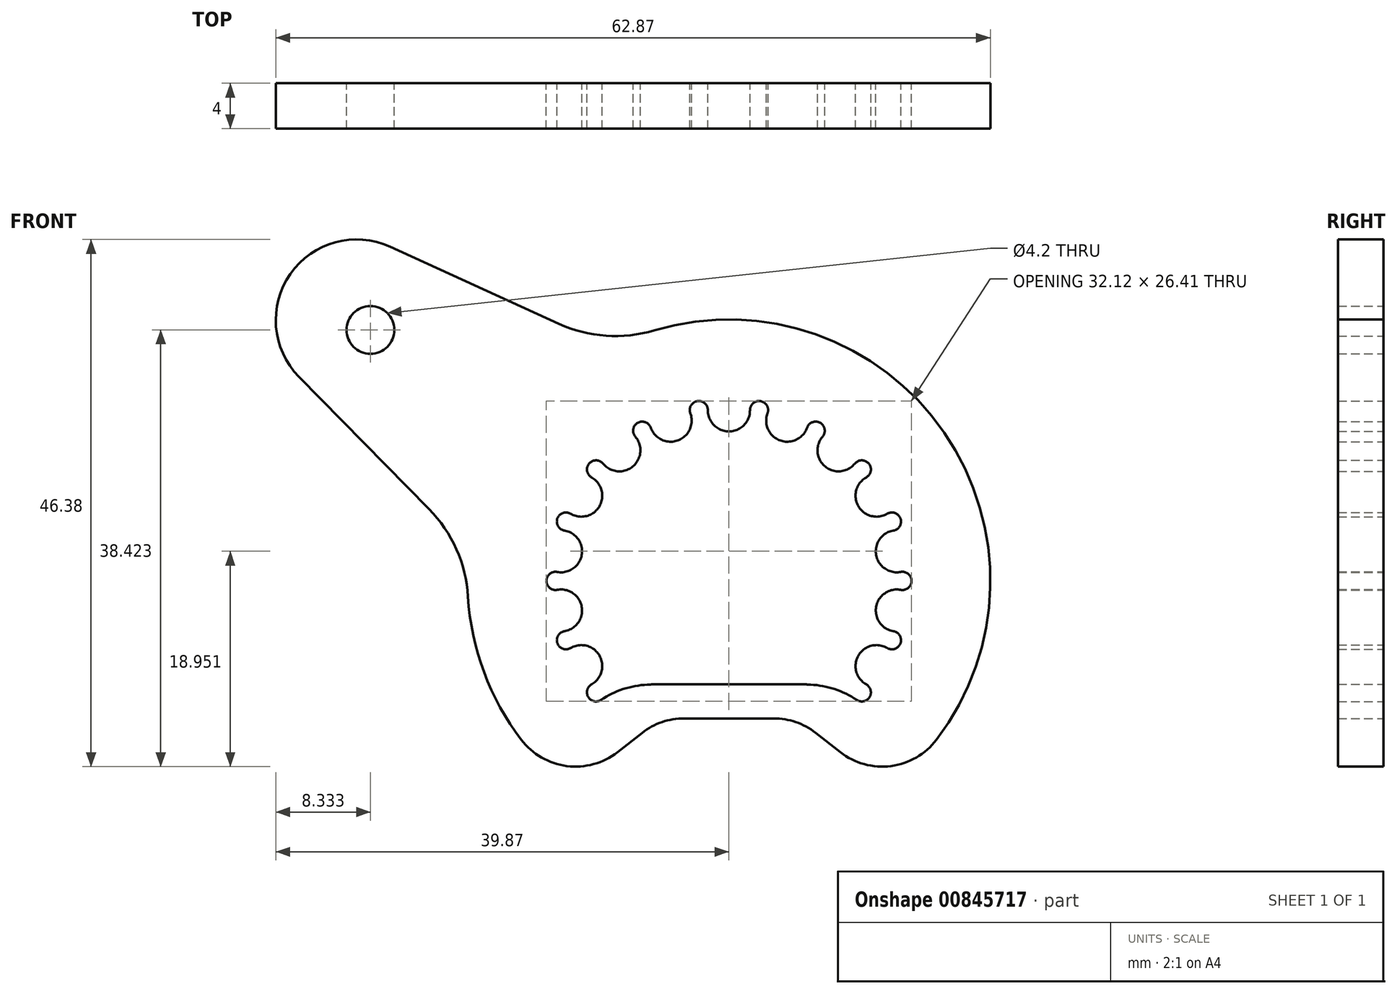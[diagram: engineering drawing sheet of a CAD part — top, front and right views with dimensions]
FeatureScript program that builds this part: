
annotation { "Feature Type Name" : "Feature", "Feature Type Description" : "" }
export const myFeature = defineFeature(function(context is Context, id is Id, definition is map)
    precondition{}
    {
        {
            var Q0;
            Q0=qCreatedBy(makeId("Front.planeOp"),FACE);
            var sketch = newSketch(context, id + "F0", { "sketchPlane" : qUnion([Q0])});
            skArc(sketch, "E0", {"start": v(-22.96, -1.37) * mm, "mid": v(-21.55, -8.03) * mm, "end": v(-18.26, -13.99) * mm});
            skLineSegment(sketch, "E1", {"start": v(-3.93, -12.1) * mm, "end": v(3.93, -12.1) * mm});
            skLineSegment(sketch, "E2", {"start": v(0, 0) * mm, "end": v(0, -12.1) * mm, "construction": true});
            skLineSegment(sketch, "E3", {"start": v(7.63, -13.37) * mm, "end": v(9.8, -15.07) * mm});
            skLineSegment(sketch, "E4", {"start": v(0, 0) * mm, "end": v(-32.77, 22.94) * mm, "construction": true});
            skLineSegment(sketch, "E5.trimOffspring", {"start": v(-28.05, 7.74) * mm, "end": v(-38.36, 14.96) * mm, "construction": true});
            skArc(sketch, "E6", {"start": v(-40.75, 28.54) * mm, "mid": v(-42.37, 21.25) * mm, "end": v(-38.36, 14.96) * mm, "construction": true});
            skArc(sketch, "E7.MirrorCS", {"start": v(-40.75, 28.54) * mm, "mid": v(-34.46, 32.54) * mm, "end": v(-27.17, 30.93) * mm, "construction": true});
            skLineSegment(sketch, "E8.MirrorCS", {"start": v(-16.87, 23.72) * mm, "end": v(-27.17, 30.93) * mm, "construction": true});
            skLineSegment(sketch, "E9.MirrorCS", {"start": v(-7.63, -13.37) * mm, "end": v(-9.8, -15.07) * mm});
            skArc(sketch, "E10.trimOffspring", {"start": v(18.26, -13.99) * mm, "mid": v(18.94, 13.05) * mm, "end": v(-6.56, 22.04) * mm});
            skLineSegment(sketch, "E11", {"start": v(-11.93, -9.1) * mm, "end": v(11.93, -9.1) * mm, "construction": true});
            skArc(sketch, "E12", {"start": v(11.43, -9.72) * mm, "mid": v(0, 15) * mm, "end": v(-11.43, -9.72) * mm, "construction": true});
            skPoint(sketch, "E13.visualSharp", {"position": v(-13.94, -18.3) * mm});
            skArc(sketch, "E13.filletArc", {"start": v(-18.26, -13.99) * mm, "mid": v(-14.25, -16.3) * mm, "end": v(-9.8, -15.07) * mm});
            skPoint(sketch, "E14.visualSharp", {"position": v(-6, -12.1) * mm});
            skArc(sketch, "E14.filletArc", {"start": v(-3.93, -12.1) * mm, "mid": v(-5.89, -12.42) * mm, "end": v(-7.63, -13.37) * mm});
            skPoint(sketch, "E15.visualSharp", {"position": v(6, -12.1) * mm});
            skArc(sketch, "E15.filletArc", {"start": v(7.63, -13.37) * mm, "mid": v(5.89, -12.42) * mm, "end": v(3.93, -12.1) * mm});
            skPoint(sketch, "E16.visualSharp", {"position": v(13.94, -18.3) * mm});
            skArc(sketch, "E16.filletArc", {"start": v(9.8, -15.07) * mm, "mid": v(14.25, -16.3) * mm, "end": v(18.26, -13.99) * mm});
            skPoint(sketch, "E17.visualSharp", {"position": v(-22.66, 3.96) * mm});
            skArc(sketch, "E17.filletArc", {"start": v(-22.96, -1.37) * mm, "mid": v(-24.46, 3.77) * mm, "end": v(-28.05, 7.74) * mm, "construction": true});
            skPoint(sketch, "E18.visualSharp", {"position": v(-11.47, 19.93) * mm});
            skArc(sketch, "E18.filletArc", {"start": v(-16.87, 23.72) * mm, "mid": v(-11.9, 21.7) * mm, "end": v(-6.56, 22.04) * mm});
            skArc(sketch, "E19", {"start": v(-30.99, 25.48) * mm, "mid": v(-35.3, 24.72) * mm, "end": v(-34.54, 20.4) * mm, "construction": true});
            skLineSegment(sketch, "E20", {"start": v(-28.43, -16.34) * mm, "end": v(42.41, -16.34) * mm, "construction": true});
            skLineSegment(sketch, "E21", {"start": v(-31.95, 22.37) * mm, "end": v(-26.35, 30.36) * mm, "construction": true});
            skArc(sketch, "E22", {"start": v(-24.72, 29.2) * mm, "mid": v(-26.21, 29.54) * mm, "end": v(-27.5, 28.72) * mm, "construction": true});
            skLineSegment(sketch, "E23", {"start": v(-32.8, 29.57) * mm, "end": v(-14.34, 29.57) * mm, "construction": true});
            skLineSegment(sketch, "E24", {"start": v(6, -12.1) * mm, "end": v(6, -9.1) * mm, "construction": true});
            skArc(sketch, "E25.trimOffspring", {"start": v(7.18, -9.13) * mm, "mid": v(6.6, -9.1) * mm, "end": v(6, -9.1) * mm});
            skArc(sketch, "E26.MirrorCS", {"start": v(-7.18, -9.13) * mm, "mid": v(-6.6, -9.1) * mm, "end": v(-6, -9.1) * mm});
            skLineSegment(sketch, "E27", {"start": v(-6, -9.1) * mm, "end": v(6, -9.1) * mm});
            skLineSegment(sketch, "E28", {"start": v(-34.54, 20.4) * mm, "end": v(-28, 15.82) * mm, "construction": true});
            skLineSegment(sketch, "E29", {"start": v(-30.99, 25.48) * mm, "end": v(-24.43, 20.9) * mm, "construction": true});
            skArc(sketch, "E30", {"start": v(-28, 15.82) * mm, "mid": v(-23.67, 16.58) * mm, "end": v(-24.43, 20.9) * mm, "construction": true});
            skArc(sketch, "E31.0", {"start": v(-29.82, 29.4) * mm, "mid": v(-38.58, 27.02) * mm, "end": v(-37.83, 17.96) * mm});
            skLineSegment(sketch, "E32", {"start": v(-37.83, 17.96) * mm, "end": v(-26.38, 6.33) * mm});
            skPoint(sketch, "E32.endSnap0", {"position": v(-24.46, 3.77) * mm});
            skPoint(sketch, "E33.orphan", {"position": v(-24.46, 4.38) * mm});
            skArc(sketch, "E34", {"start": v(-22.96, -1.37) * mm, "mid": v(-23.97, 2.79) * mm, "end": v(-26.38, 6.33) * mm});
            skLineSegment(sketch, "E35.MirrorCS", {"start": v(-29.82, 29.4) * mm, "end": v(-14.97, 22.63) * mm});
            skArc(sketch, "E36.MirrorCS", {"start": v(-6.56, 22.04) * mm, "mid": v(-10.82, 21.57) * mm, "end": v(-14.97, 22.63) * mm, "construction": true});
            skPoint(sketch, "E37.orphan", {"position": v(-16.87, 23.72) * mm});
            skLineSegment(sketch, "E38", {"start": v(0, 0) * mm, "end": v(13, -7.5) * mm, "construction": true});
            skArc(sketch, "E39", {"start": v(13.93, -5.9) * mm, "mid": v(11.39, -6.58) * mm, "end": v(12.08, -9.11) * mm});
            skLineSegment(sketch, "E40", {"start": v(0, 0) * mm, "end": v(14.77, -2.6) * mm, "construction": true});
            skArc(sketch, "E41", {"start": v(15.11, -0.79) * mm, "mid": v(12.95, -2.28) * mm, "end": v(14.47, -4.43) * mm});
            skArc(sketch, "E42", {"start": v(13.93, -5.9) * mm, "mid": v(15.1, -5.5) * mm, "end": v(14.47, -4.43) * mm});
            skArc(sketch, "E43", {"start": v(13.3, -5.67) * mm, "mid": v(14.17, -5.16) * mm, "end": v(13.83, -4.2) * mm, "construction": true});
            skArc(sketch, "E44.MirrorCS", {"start": v(12.08, -9.11) * mm, "mid": v(12.37, -10.23) * mm, "end": v(11.24, -10.47) * mm});
            skArc(sketch, "E45.MirrorCS", {"start": v(15.11, 0.79) * mm, "mid": v(16.06, 0) * mm, "end": v(15.11, -0.79) * mm});
            skPoint(sketch, "E46.orphan", {"position": v(11.07, -10.32) * mm});
            skPoint(sketch, "E47.visualSharp", {"position": v(10.92, -9.6) * mm});
            skArc(sketch, "E47.filletArc", {"start": v(11.24, -10.47) * mm, "mid": v(9.3, -9.52) * mm, "end": v(7.18, -9.13) * mm});
            skLineSegment(sketch, "E48", {"start": v(0, 0) * mm, "end": v(14.77, 2.6) * mm, "construction": true});
            skLineSegment(sketch, "E49", {"start": v(0, 0) * mm, "end": v(13, 7.5) * mm, "construction": true});
            skLineSegment(sketch, "E50", {"start": v(9.64, 11.5) * mm, "end": v(0, 0) * mm, "construction": true});
            skLineSegment(sketch, "E51", {"start": v(0, 0) * mm, "end": v(5.13, 14.1) * mm, "construction": true});
            skArc(sketch, "E52.MirrorCS", {"start": v(13.93, 5.9) * mm, "mid": v(11.39, 6.57) * mm, "end": v(12.08, 9.11) * mm});
            skArc(sketch, "E53.MirrorCS", {"start": v(14.47, 4.43) * mm, "mid": v(15.1, 5.5) * mm, "end": v(13.93, 5.9) * mm});
            skArc(sketch, "E54.MirrorCS", {"start": v(11.07, 10.32) * mm, "mid": v(12.3, 10.32) * mm, "end": v(12.08, 9.11) * mm});
            skArc(sketch, "E55.MirrorCS", {"start": v(11.07, 10.32) * mm, "mid": v(8.45, 10.07) * mm, "end": v(8.24, 12.7) * mm});
            skArc(sketch, "E56.MirrorCS", {"start": v(15.11, 0.79) * mm, "mid": v(12.95, 2.28) * mm, "end": v(14.47, 4.43) * mm});
            skArc(sketch, "E57.MirrorCS", {"start": v(8.24, 12.7) * mm, "mid": v(8.03, 13.9) * mm, "end": v(6.88, 13.48) * mm});
            skArc(sketch, "E58.MirrorCS", {"start": v(3.4, 14.75) * mm, "mid": v(4.5, 12.36) * mm, "end": v(6.88, 13.48) * mm});
            skArc(sketch, "E59.MirrorCS", {"start": v(1.85, 15.02) * mm, "mid": v(2.79, 15.82) * mm, "end": v(3.4, 14.75) * mm});
            skArc(sketch, "E60.MirrorCS", {"start": v(-1.85, 15.02) * mm, "mid": v(0, 13.15) * mm, "end": v(1.85, 15.02) * mm});
            skArc(sketch, "E61.MirrorCS", {"start": v(-1.85, 15.02) * mm, "mid": v(-2.79, 15.82) * mm, "end": v(-3.4, 14.75) * mm});
            skArc(sketch, "E62.MirrorCS", {"start": v(-3.4, 14.75) * mm, "mid": v(-4.5, 12.36) * mm, "end": v(-6.88, 13.48) * mm});
            skArc(sketch, "E63.MirrorCS", {"start": v(-8.24, 12.7) * mm, "mid": v(-8.03, 13.9) * mm, "end": v(-6.88, 13.48) * mm});
            skArc(sketch, "E64.MirrorCS", {"start": v(-11.07, 10.32) * mm, "mid": v(-8.45, 10.07) * mm, "end": v(-8.24, 12.7) * mm});
            skArc(sketch, "E65.MirrorCS", {"start": v(-11.07, 10.32) * mm, "mid": v(-12.3, 10.32) * mm, "end": v(-12.08, 9.11) * mm});
            skArc(sketch, "E66.MirrorCS", {"start": v(-13.93, 5.9) * mm, "mid": v(-11.39, 6.57) * mm, "end": v(-12.08, 9.11) * mm});
            skArc(sketch, "E67.MirrorCS", {"start": v(-14.47, 4.43) * mm, "mid": v(-15.1, 5.5) * mm, "end": v(-13.93, 5.9) * mm});
            skArc(sketch, "E68.MirrorCS", {"start": v(-15.11, 0.79) * mm, "mid": v(-12.95, 2.28) * mm, "end": v(-14.47, 4.43) * mm});
            skArc(sketch, "E69.MirrorCS", {"start": v(-15.11, 0.79) * mm, "mid": v(-16.06, 0) * mm, "end": v(-15.11, -0.79) * mm});
            skArc(sketch, "E70.MirrorCS", {"start": v(-15.11, -0.79) * mm, "mid": v(-12.95, -2.28) * mm, "end": v(-14.47, -4.43) * mm});
            skArc(sketch, "E71.MirrorCS", {"start": v(-13.93, -5.9) * mm, "mid": v(-15.1, -5.5) * mm, "end": v(-14.47, -4.43) * mm});
            skArc(sketch, "E72.MirrorCS", {"start": v(-13.93, -5.9) * mm, "mid": v(-11.39, -6.58) * mm, "end": v(-12.08, -9.11) * mm});
            skArc(sketch, "E73.MirrorCS", {"start": v(-12.08, -9.11) * mm, "mid": v(-12.37, -10.23) * mm, "end": v(-11.24, -10.47) * mm});
            skArc(sketch, "E74.MirrorCS", {"start": v(-11.24, -10.47) * mm, "mid": v(-9.3, -9.52) * mm, "end": v(-7.18, -9.13) * mm});
            skPoint(sketch, "E75.orphan", {"position": v(-11.43, -9.72) * mm});
            skCircle(sketch, "E76", {"center": v(-31.54, 22.08) * mm, "radius": 2.1 * mm});
            skSolve(sketch);
        }
        {
            var Q0;
            Q0=makeQuery(id+"F0.imprint","IMPRINT",FACE,{"disambiguationData":[TD([[makeQuery(id+"F0.imprint","IMPRINT",EDGE,{"derivedFrom":sQuery(id+"F0.wireOp",EDGE,"E0")}),1.0]])]});
            extrude(context, id + "F1", {"entities" : qUnion([Q0]), "depth" : 4 * mm, "offsetDistance" : 25 * mm});
        }
    });
